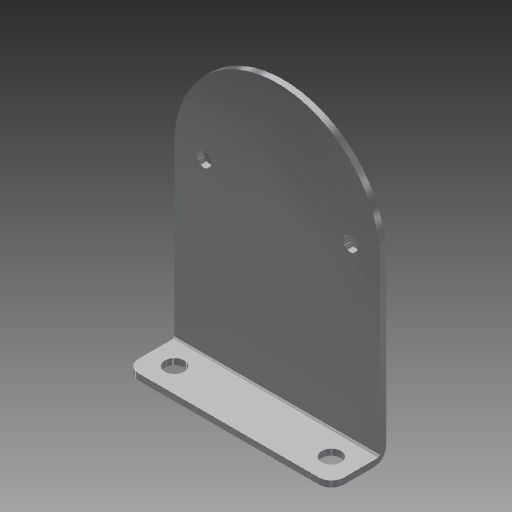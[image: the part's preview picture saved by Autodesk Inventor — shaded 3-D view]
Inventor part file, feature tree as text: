
AUTODESK INVENTOR PART (.ipt)
format: ipt  version: 2017.1 (Build 211199000, 199)  size: 137,728 bytes
history: native  units: in
note: dims shown in document units (in); Inventor stores cm internally (conversion verified against a paired STEP export)
features: fillet x3, hole x3, sketch x3, extrude x2, reference x2
ambient origin geometry x8: Origin, YZ Plane, XZ Plane, XY Plane, X Axis, Y Axis, Z Axis, Center Point
bodies: Solid1 (feature_tree)
feature tree (13):
  extrude  "Extrusion1"  Depth=0.0625in
  extrude  "Extrusion2"  Depth=0.125in
  fillet  "Fillet1"  Radius=0.0312in
  hole  "Hole1"  [1 undecoded]
  fillet  "Fillet2"  Radius=0.75in
  hole  "Hole2"  [1 undecoded]
  hole  "Hole3"  [1 undecoded]
  fillet  "Fillet3"  [1 undecoded]
  sketch  "Sketch1"  dims[d0=0.0625in d1=0.0in d2=0.0625in]
  reference  "Reference1"
  sketch  "Sketch2"  dims[d3=0.5in d4=0.0in d5=0.125in]
  sketch  "Sketch3"  dims[d6=0.25in d16=0.25in d8=0.201in d9=0.75in d10=0.385in d11=0.25in d12=0.5635in d13=1.0in d14=0.8108in d15=0.0312in d17=0.25in d18=0.25in d19=0.201in d20=0.75in d21=0.385in d22=0.25in d23=0.5635in d24=1.0in d25=0.8108in d26=0.75in d27=0.75in d28=0.15in d29=0.75in d30=0.385in d31=0.25in d32=0.5635in d33=1.0in d34=0.8108in d35=0.125in]
  reference  "Reference3"
note: 4 required parameter values undecoded (feature->parameter linkage not recoverable at this tier; creation-order binding heuristic only, values carry confidence <= 0.55)
